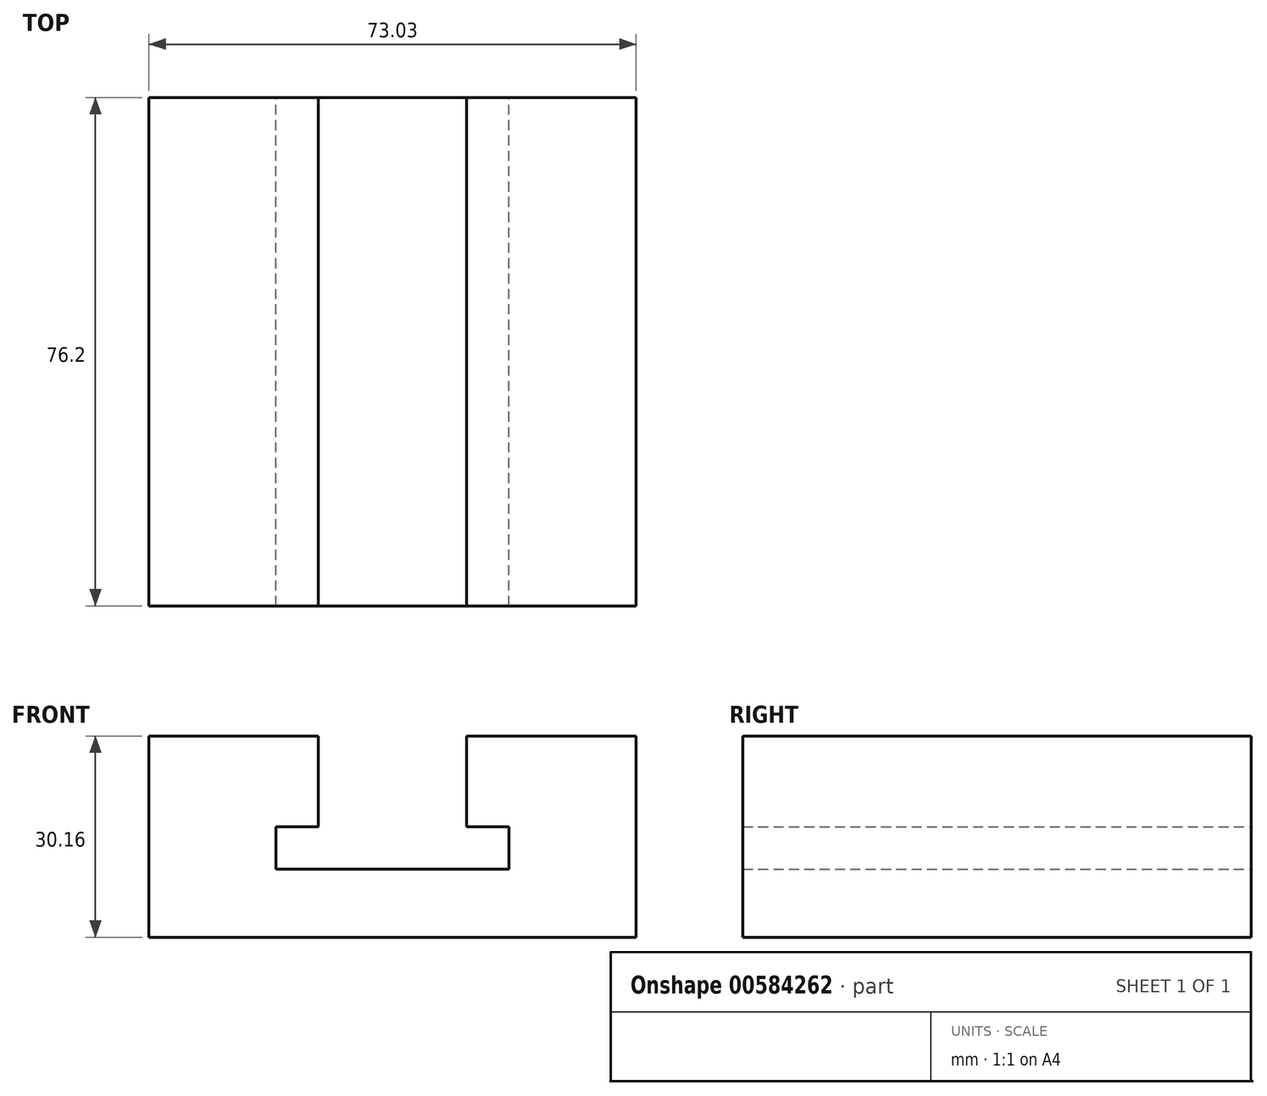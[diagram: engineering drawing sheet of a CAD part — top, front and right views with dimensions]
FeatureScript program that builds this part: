
annotation { "Feature Type Name" : "Feature", "Feature Type Description" : "" }
export const myFeature = defineFeature(function(context is Context, id is Id, definition is map)
    precondition{}
    {
        {
            var Q0;
            Q0=qCreatedBy(makeId("Front.planeOp"),FACE);
            var sketch = newSketch(context, id + "F0", { "sketchPlane" : qUnion([Q0])});
            skLineSegment(sketch, "E0", {"start": v(0, 0) * mm, "end": v(73.03, 0) * mm});
            skLineSegment(sketch, "E1", {"start": v(73.03, 0) * mm, "end": v(73.03, 30.16) * mm});
            skLineSegment(sketch, "E2", {"start": v(73.03, 30.16) * mm, "end": v(47.62, 30.16) * mm});
            skLineSegment(sketch, "E3", {"start": v(47.63, 30.16) * mm, "end": v(47.63, 16.52) * mm});
            skLineSegment(sketch, "E4", {"start": v(47.62, 16.52) * mm, "end": v(53.98, 16.52) * mm});
            skLineSegment(sketch, "E5", {"start": v(53.98, 16.52) * mm, "end": v(53.98, 10.17) * mm});
            skLineSegment(sketch, "E6", {"start": v(53.98, 10.17) * mm, "end": v(19.05, 10.17) * mm});
            skLineSegment(sketch, "E7", {"start": v(19.05, 10.17) * mm, "end": v(19.05, 16.52) * mm});
            skLineSegment(sketch, "E8", {"start": v(19.05, 16.52) * mm, "end": v(25.4, 16.52) * mm});
            skLineSegment(sketch, "E9", {"start": v(25.4, 16.52) * mm, "end": v(25.4, 30.16) * mm});
            skLineSegment(sketch, "E10", {"start": v(25.4, 30.16) * mm, "end": v(0, 30.16) * mm});
            skLineSegment(sketch, "E11", {"start": v(0, 30.16) * mm, "end": v(0, 0) * mm});
            skSolve(sketch);
        }
        {
            var Q0;
            Q0=makeQuery(id+"F0.imprint","IMPRINT",FACE,{"disambiguationData":[TD([[makeQuery(id+"F0.imprint","IMPRINT",EDGE,{"derivedFrom":sQuery(id+"F0.wireOp",EDGE,"E0")}),1.0]])]});
            extrude(context, id + "F1", {"entities" : qUnion([Q0]), "depth" : 76.2 * mm, "offsetDistance" : 25.4 * mm});
        }
    });
